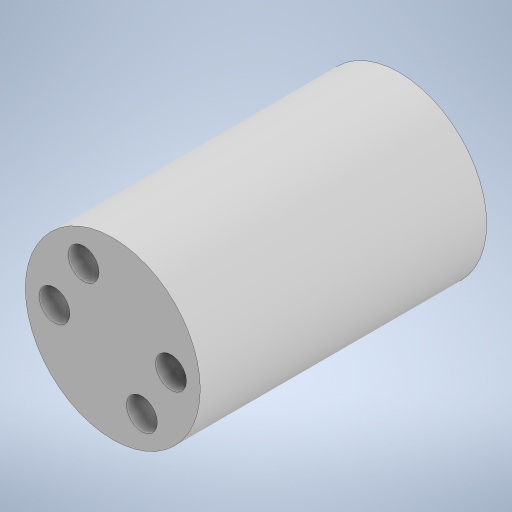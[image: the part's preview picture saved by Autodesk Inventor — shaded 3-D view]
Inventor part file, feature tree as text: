
AUTODESK INVENTOR PART (.ipt)
format: ipt  version: 2023 (Build 270158000, 158)  size: 225,280 bytes
history: native  units: in
note: dims shown in document units (in); Inventor stores cm internally (conversion verified against a paired STEP export)
features: extrude x1, sketch x1
ambient origin geometry x8: Origin, YZ Plane, XZ Plane, XY Plane, X Axis, Y Axis, Z Axis, Center Point
bodies: Body1 (feature_tree)
feature tree (2):
  extrude  "Extrusion14"  Depth=1.228in
  sketch  "Sketch1"  dims[d3=0.866in d15=0.75in d37=0.75in d69=0.132in d70=0.132in d73=1.228in d74=0.0in d75=0.132in d76=0.132in d77=0.132in d78=0.132in]
